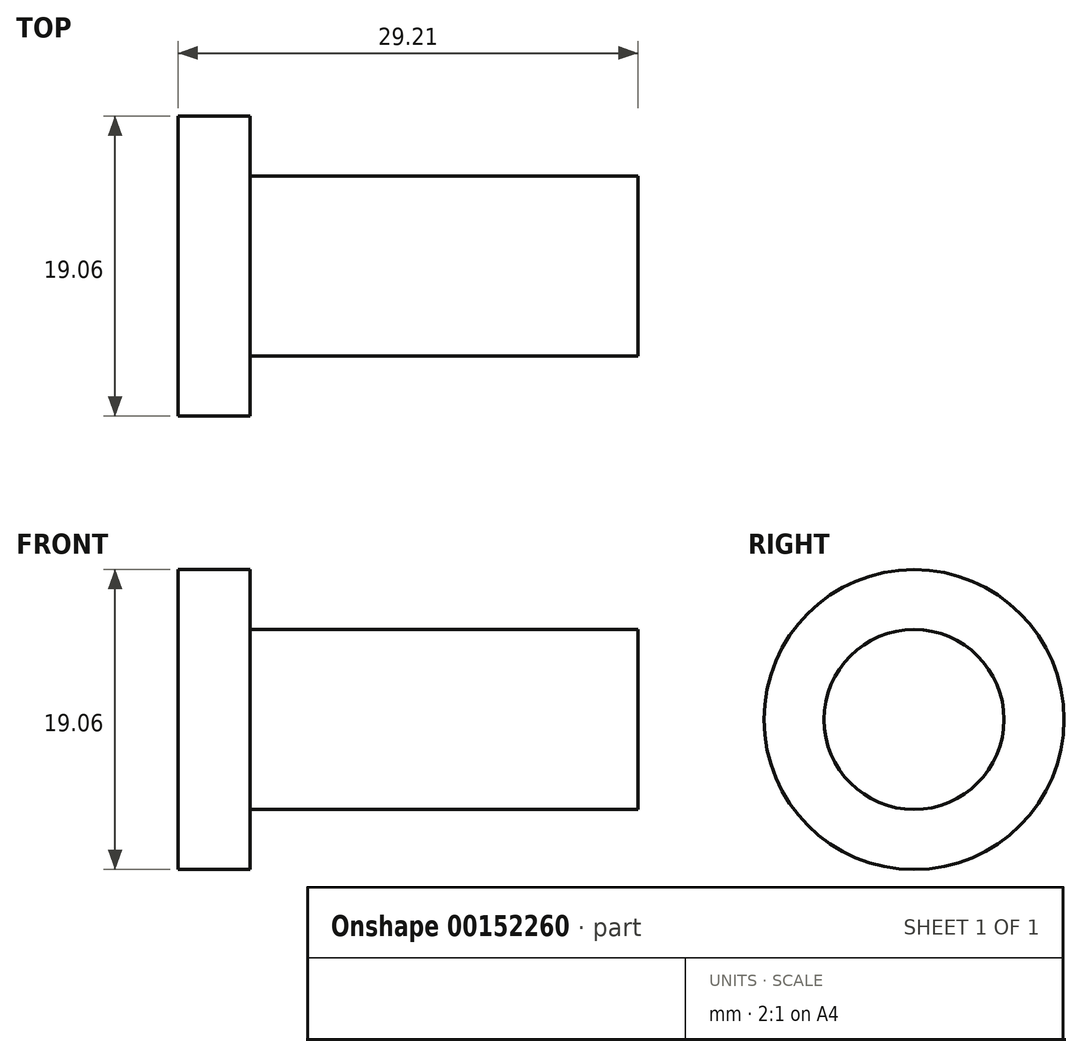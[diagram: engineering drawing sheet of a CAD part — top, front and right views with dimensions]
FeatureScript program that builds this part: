
annotation { "Feature Type Name" : "Feature", "Feature Type Description" : "" }
export const myFeature = defineFeature(function(context is Context, id is Id, definition is map)
    precondition{}
    {
        {
            var Q0;
            Q0=qCreatedBy(makeId("Front.planeOp"),FACE);
            var sketch = newSketch(context, id + "F0", { "sketchPlane" : qUnion([Q0])});
            skLineSegment(sketch, "E0", {"start": v(0, 0) * mm, "end": v(0, 9.52) * mm});
            skLineSegment(sketch, "E1", {"start": v(0, 9.52) * mm, "end": v(4.57, 9.52) * mm});
            skLineSegment(sketch, "E2", {"start": v(4.57, 9.52) * mm, "end": v(4.57, 5.71) * mm});
            skLineSegment(sketch, "E3", {"start": v(4.57, 5.71) * mm, "end": v(29.21, 5.71) * mm});
            skLineSegment(sketch, "E4", {"start": v(29.21, 5.71) * mm, "end": v(29.21, 0) * mm});
            skLineSegment(sketch, "E5", {"start": v(29.21, 0) * mm, "end": v(0, 0) * mm});
            skSolve(sketch);
        }
        {
            var Q0;
            Q0 = qSketchRegion(id + "F0", true);
            var Q1;
            Q1=sQuery(id+"F0.wireOp",EDGE,"E5");
            revolve(context, id + "F1", {"entities" : qUnion([Q0]), "axis" : qUnion([Q1]), "revolveType" : RevolveType.FULL});
        }
    });
